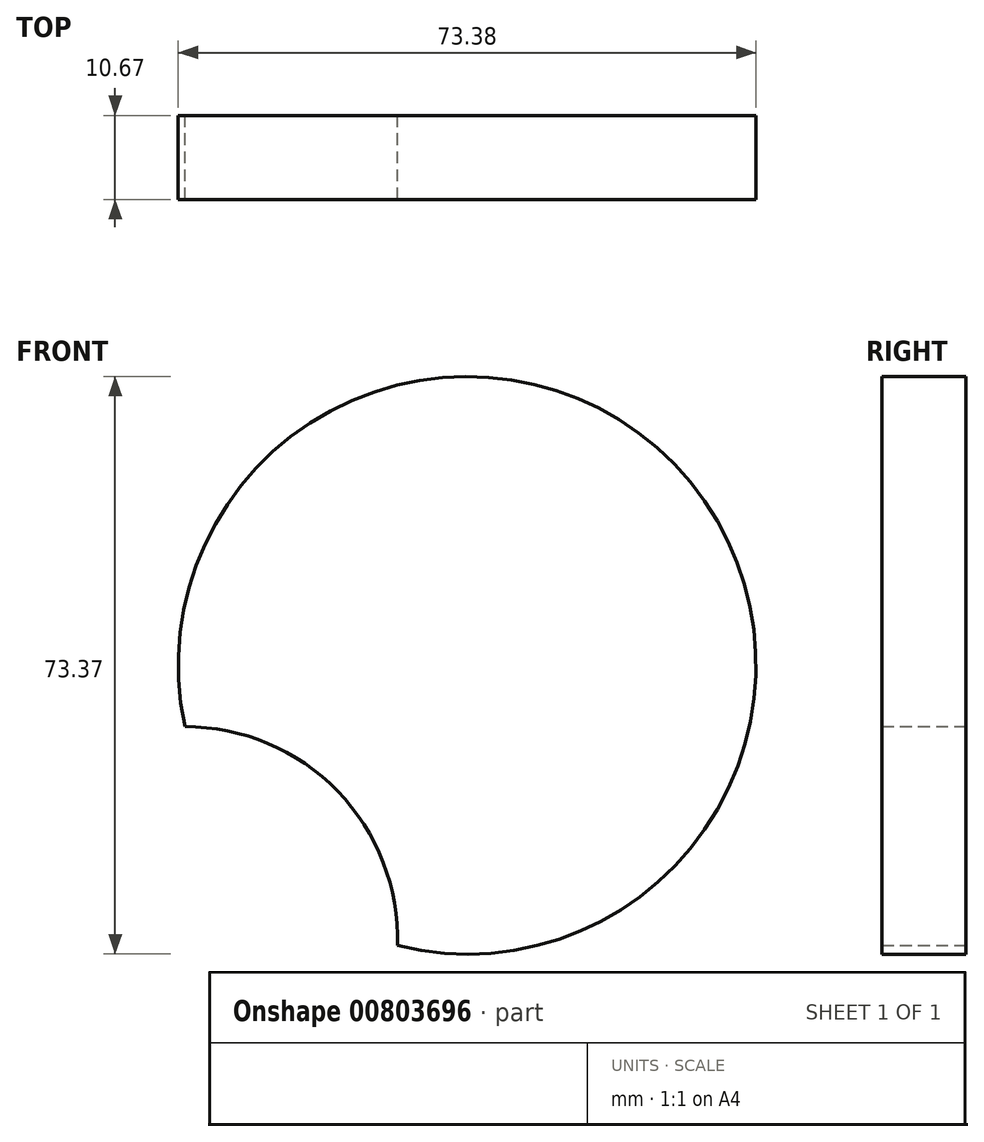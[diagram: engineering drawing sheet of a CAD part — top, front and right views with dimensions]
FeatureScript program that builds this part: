
annotation { "Feature Type Name" : "Feature", "Feature Type Description" : "" }
export const myFeature = defineFeature(function(context is Context, id is Id, definition is map)
    precondition{}
    {
        {
            var Q0;
            Q0=qCreatedBy(makeId("Front.planeOp"),FACE);
            var sketch = newSketch(context, id + "F0", { "sketchPlane" : qUnion([Q0])});
            skArc(sketch, "E0", {"start": v(27, 0) * mm, "mid": v(62.18, 61.16) * mm, "end": v(0, 27.81) * mm});
            skArc(sketch, "E1", {"start": v(27, 0) * mm, "mid": v(19.39, 19.62) * mm, "end": v(0, 27.81) * mm});
            skSolve(sketch);
        }
        {
            var Q0;
            Q0=makeQuery(id+"F0.imprint","IMPRINT",FACE,{"disambiguationData":[TD([[makeQuery(id+"F0.imprint","IMPRINT",EDGE,{"derivedFrom":sQuery(id+"F0.wireOp",EDGE,"E0")}),1.0]])]});
            extrude(context, id + "F1", {"entities" : qUnion([Q0]), "depth" : 5.33 * mm, "offsetDistance" : 25.4 * mm});
        }
        {
            var Q0;
            Q0=makeQuery(id+"F1.opExtrude","CAP_FACE",FACE,{"disambiguationData":[OSD([sQuery(id+"F0.wireOp",EDGE,"E0"),sQuery(id+"F0.wireOp",EDGE,"E1")])],"isStart":false});
            extrude(context, id + "F2", {"entities" : qUnion([Q0]), "operationType" : NewBodyOperationType.ADD, "depth" : 5.33 * mm, "offsetDistance" : 25.4 * mm});
        }
    });
